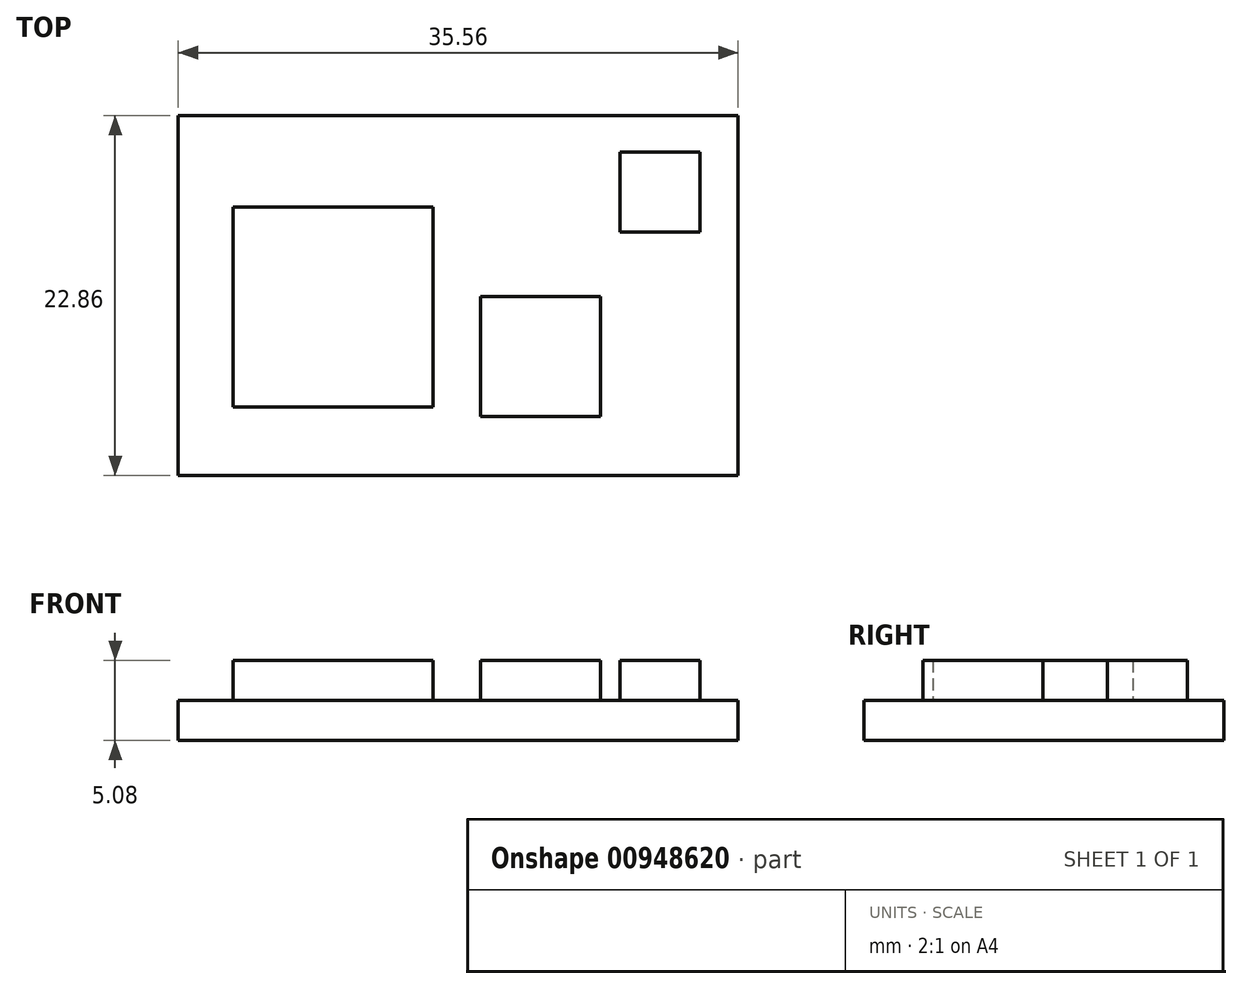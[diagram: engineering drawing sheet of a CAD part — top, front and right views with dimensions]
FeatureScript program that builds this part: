
annotation { "Feature Type Name" : "Feature", "Feature Type Description" : "" }
export const myFeature = defineFeature(function(context is Context, id is Id, definition is map)
    precondition{}
    {
        {
            var Q0;
            Q0=qCreatedBy(makeId("Top.planeOp"),FACE);
            var sketch = newSketch(context, id + "F0", { "sketchPlane" : qUnion([Q0])});
            skLineSegment(sketch, "E0.bottom", {"start": v(-4.21, 3.24) * mm, "end": v(31.35, 3.24) * mm});
            skLineSegment(sketch, "E0.top", {"start": v(-4.21, -19.62) * mm, "end": v(31.35, -19.62) * mm});
            skLineSegment(sketch, "E0.left", {"start": v(-4.21, 3.24) * mm, "end": v(-4.21, -19.62) * mm});
            skLineSegment(sketch, "E0.right", {"start": v(31.35, 3.24) * mm, "end": v(31.35, -19.62) * mm});
            skSolve(sketch);
        }
        {
            var Q0;
            Q0 = qSketchRegion(id + "F0", true);
            extrude(context, id + "F1", {"entities" : qUnion([Q0]), "depth" : 2.54 * mm, "offsetDistance" : 25.4 * mm});
        }
        {
            var Q0;
            Q0=makeQuery(id+"F1.opExtrude","CAP_FACE",FACE,{"disambiguationData":[OSD([sQuery(id+"F0.wireOp",EDGE,"E0.bottom"),sQuery(id+"F0.wireOp",EDGE,"E0.top"),sQuery(id+"F0.wireOp",EDGE,"E0.left"),sQuery(id+"F0.wireOp",EDGE,"E0.right")])],"isStart":false});
            var sketch = newSketch(context, id + "F2", { "sketchPlane" : qUnion([Q0])});
            skLineSegment(sketch, "E1.bottom", {"start": v(28.94, 0.92) * mm, "end": v(23.86, 0.92) * mm});
            skLineSegment(sketch, "E1.top", {"start": v(28.94, -4.16) * mm, "end": v(23.86, -4.16) * mm});
            skLineSegment(sketch, "E1.left", {"start": v(28.94, 0.92) * mm, "end": v(28.94, -4.16) * mm});
            skLineSegment(sketch, "E1.right", {"start": v(23.86, 0.92) * mm, "end": v(23.86, -4.16) * mm});
            skLineSegment(sketch, "E2.bottom", {"start": v(22.6, -8.25) * mm, "end": v(14.98, -8.25) * mm});
            skLineSegment(sketch, "E2.top", {"start": v(22.6, -15.87) * mm, "end": v(14.98, -15.87) * mm});
            skLineSegment(sketch, "E2.left", {"start": v(22.6, -8.25) * mm, "end": v(22.6, -15.87) * mm});
            skLineSegment(sketch, "E2.right", {"start": v(14.98, -8.25) * mm, "end": v(14.98, -15.87) * mm});
            skLineSegment(sketch, "E3.bottom", {"start": v(-0.74, -15.26) * mm, "end": v(11.96, -15.26) * mm});
            skLineSegment(sketch, "E3.top", {"start": v(-0.74, -2.56) * mm, "end": v(11.96, -2.56) * mm});
            skLineSegment(sketch, "E3.left", {"start": v(-0.74, -15.26) * mm, "end": v(-0.74, -2.56) * mm});
            skLineSegment(sketch, "E3.right", {"start": v(11.96, -15.26) * mm, "end": v(11.96, -2.56) * mm});
            skSolve(sketch);
        }
        {
            var Q0;
            Q0 = qSketchRegion(id + "F2", true);
            extrude(context, id + "F3", {"entities" : qUnion([Q0]), "depth" : 2.54 * mm, "offsetDistance" : 25.4 * mm});
        }
    });
